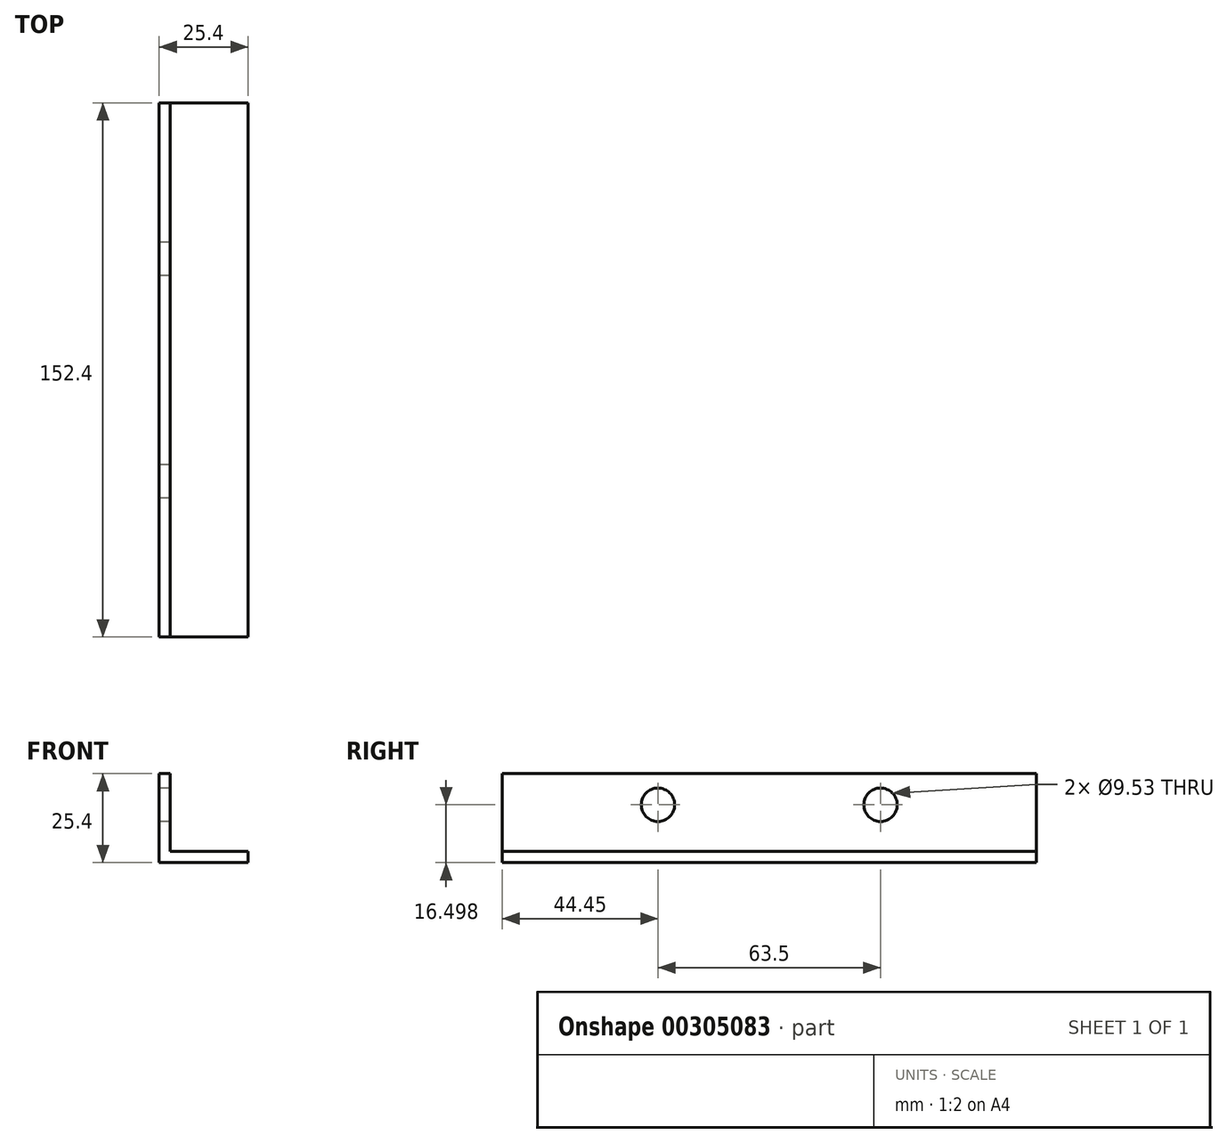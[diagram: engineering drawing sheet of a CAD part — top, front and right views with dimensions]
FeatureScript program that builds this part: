
annotation { "Feature Type Name" : "Feature", "Feature Type Description" : "" }
export const myFeature = defineFeature(function(context is Context, id is Id, definition is map)
    precondition{}
    {
        {
            var Q0;
            Q0=qCreatedBy(makeId("Front.planeOp"),FACE);
            var sketch = newSketch(context, id + "F0", { "sketchPlane" : qUnion([Q0])});
            skLineSegment(sketch, "E0", {"start": v(0, 25.4) * mm, "end": v(0, 0) * mm});
            skLineSegment(sketch, "E1", {"start": v(0, 0) * mm, "end": v(25.4, 0) * mm});
            skLineSegment(sketch, "E2", {"start": v(25.4, 0) * mm, "end": v(25.4, 3.18) * mm});
            skLineSegment(sketch, "E3", {"start": v(25.4, 3.18) * mm, "end": v(3.18, 3.17) * mm});
            skLineSegment(sketch, "E4", {"start": v(3.18, 3.17) * mm, "end": v(3.18, 25.4) * mm});
            skLineSegment(sketch, "E5", {"start": v(3.18, 25.4) * mm, "end": v(0, 25.4) * mm});
            skSolve(sketch);
        }
        {
            var Q0;
            Q0=makeQuery(id+"F0.imprint","IMPRINT",FACE,{"disambiguationData":[TD([[makeQuery(id+"F0.imprint","IMPRINT",EDGE,{"derivedFrom":sQuery(id+"F0.wireOp",EDGE,"E0")}),1.0]])]});
            extrude(context, id + "F1", {"entities" : qUnion([Q0]), "depth" : 152.4 * mm});
        }
        {
            var Q0;
            Q0=makeQuery(id+"F1.opExtrude","SWEPT_FACE",FACE,{"disambiguationData":[OSD([sQuery(id+"F0.wireOp",EDGE,"E0")])]});
            var sketch = newSketch(context, id + "F2", { "sketchPlane" : qUnion([Q0])});
            skPoint(sketch, "E6", {"position": v(44.45, 16.5) * mm});
            skPoint(sketch, "E7", {"position": v(107.95, 16.5) * mm});
            skLineSegment(sketch, "E8.0", {"start": v(152.4, 25.4) * mm, "end": v(0, 25.4) * mm});
            skSolve(sketch);
        }
        {
            var Q0;
            Q0=sQuery(id+"F2.wireOp",VERTEX,"E6");
            var Q1;
            Q1=sQuery(id+"F2.wireOp",VERTEX,"E7");
            var Q2;
            Q2=makeQuery(id+"F1.opExtrude","SWEPT_BODY",BODY,{"disambiguationData":[OSD([sQuery(id+"F0.wireOp",EDGE,"E0"),sQuery(id+"F0.wireOp",EDGE,"E1"),sQuery(id+"F0.wireOp",EDGE,"E2"),sQuery(id+"F0.wireOp",EDGE,"E3"),sQuery(id+"F0.wireOp",EDGE,"E4"),sQuery(id+"F0.wireOp",EDGE,"E5")])]});
            hole(context, id + "F3", {"style" : HoleStyle.SIMPLE, "endStyle" : HoleEndStyle.THROUGH, "holeDiameter" : 9.52 * mm, "tappedDepth" : 12.7 * mm, "tapClearance" : 3, "locations" : qUnion([Q0, Q1]), "scope" : qUnion([Q2])});
        }
    });
